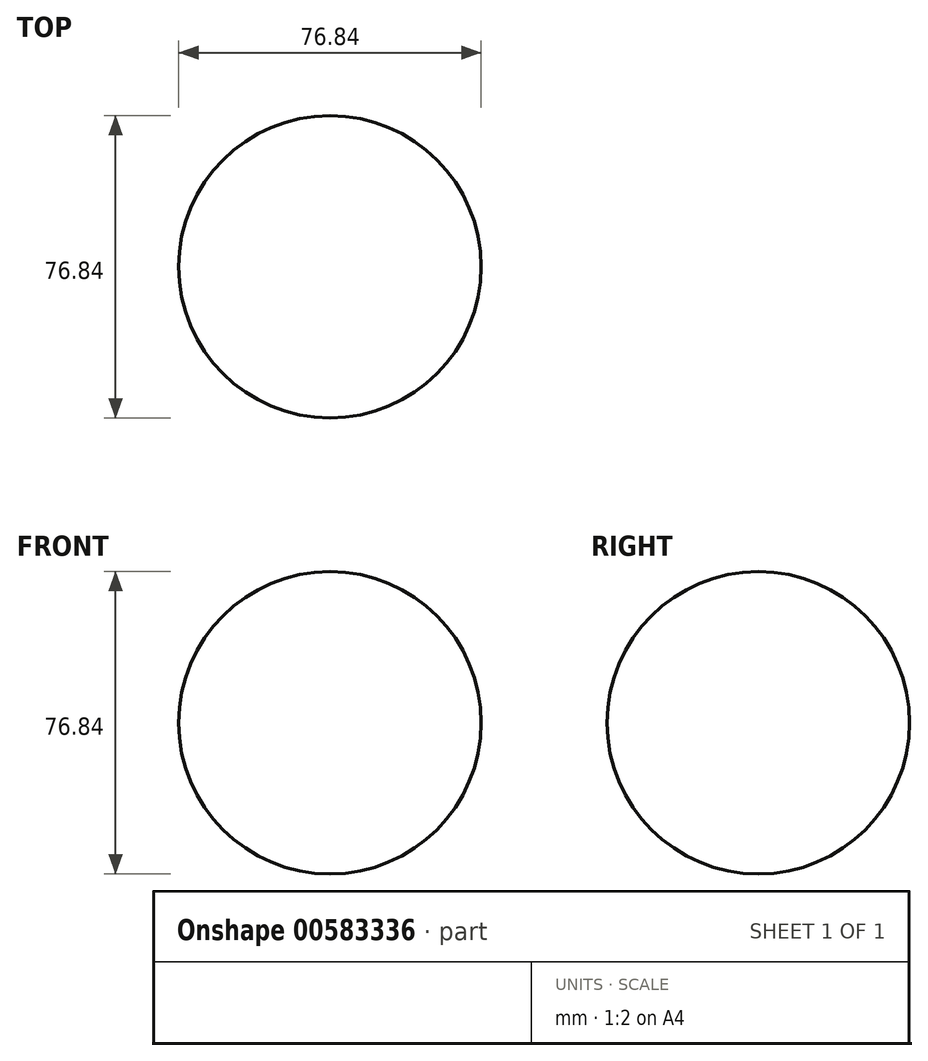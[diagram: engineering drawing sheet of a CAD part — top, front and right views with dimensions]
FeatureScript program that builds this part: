
annotation { "Feature Type Name" : "Feature", "Feature Type Description" : "" }
export const myFeature = defineFeature(function(context is Context, id is Id, definition is map)
    precondition{}
    {
        {
            var Q0;
            Q0=qCreatedBy(makeId("Front.planeOp"),FACE);
            var sketch = newSketch(context, id + "F0", { "sketchPlane" : qUnion([Q0])});
            skCircle(sketch, "E0", {"center": v(0, 0) * mm, "radius": 38.42 * mm});
            skLineSegment(sketch, "E1", {"start": v(0, -38.42) * mm, "end": v(0, 38.42) * mm});
            skSolve(sketch);
        }
        {
            var Q0;
            {var subQ0=sQuery(id+"F0.wireOp",EDGE,"E1");Q0=makeQuery(id+"F0.imprint","IMPRINT",FACE,{"disambiguationData":[TD([[makeQuery(id+"F0.imprint","IMPRINT",EDGE,{"derivedFrom":subQ0}),-1.0]])]});}
            var Q1;
            Q1=sQuery(id+"F0.wireOp",EDGE,"E1");
            revolve(context, id + "F1", {"entities" : qUnion([Q0]), "axis" : qUnion([Q1]), "revolveType" : RevolveType.FULL});
        }
    });
